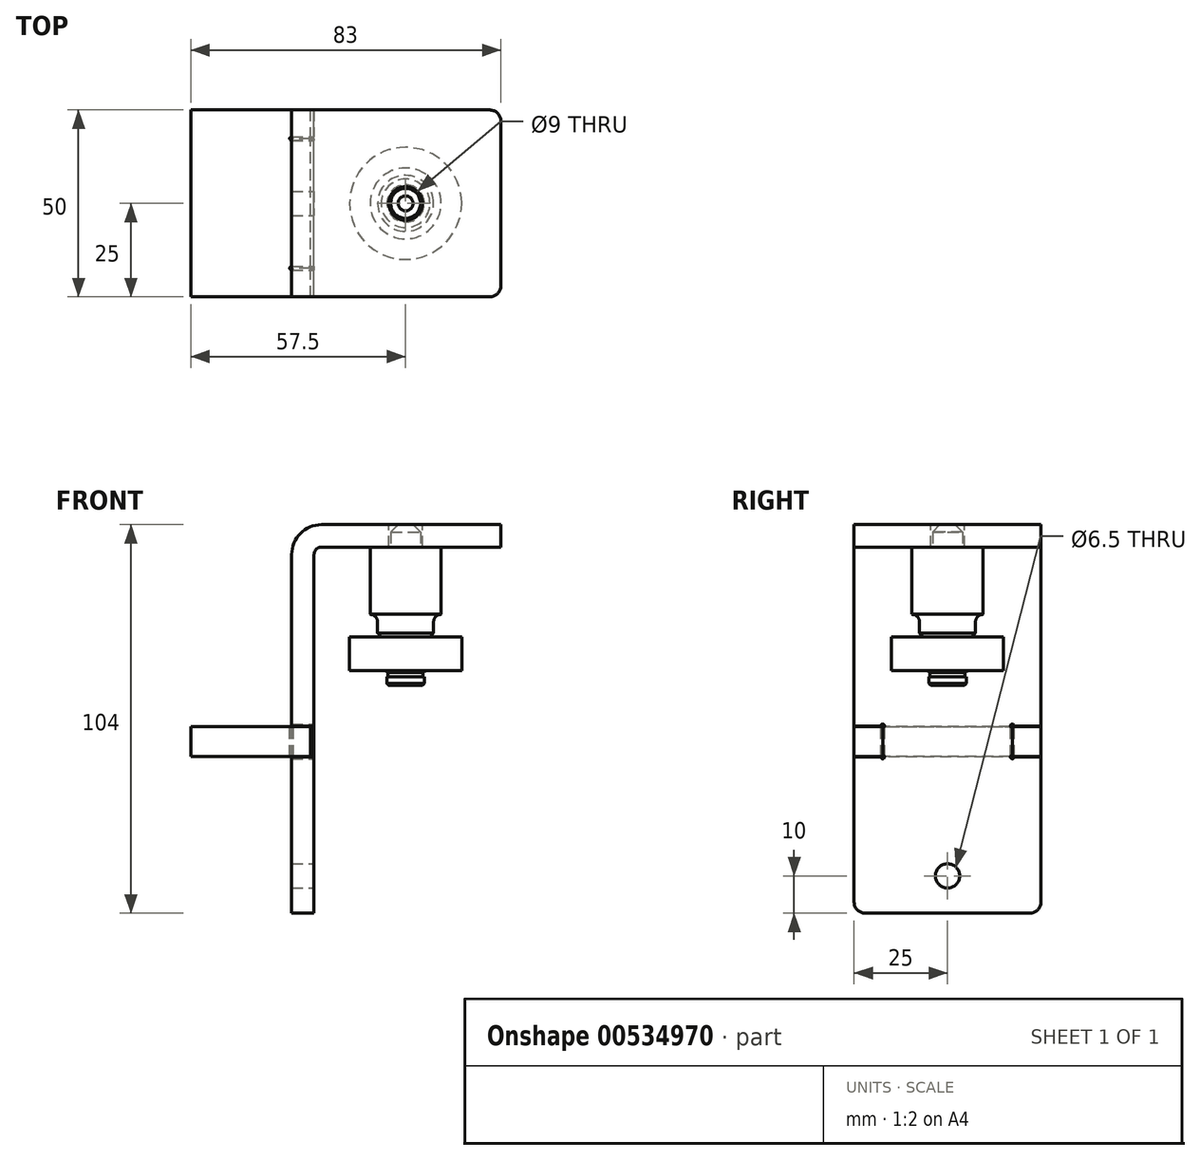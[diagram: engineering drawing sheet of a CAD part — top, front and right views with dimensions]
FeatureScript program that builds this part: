
annotation { "Feature Type Name" : "Feature", "Feature Type Description" : "" }
export const myFeature = defineFeature(function(context is Context, id is Id, definition is map)
    precondition{}
    {
        {
            var Q0;
            Q0=qCreatedBy(makeId("Front.planeOp"),FACE);
            var sketch = newSketch(context, id + "F0", { "sketchPlane" : qUnion([Q0])});
            skLineSegment(sketch, "E0", {"start": v(0, 0) * mm, "end": v(0, 96) * mm});
            skLineSegment(sketch, "E1", {"start": v(8, 104) * mm, "end": v(56, 104) * mm});
            skLineSegment(sketch, "E2", {"start": v(56, 104) * mm, "end": v(56, 98) * mm});
            skLineSegment(sketch, "E3", {"start": v(56, 98) * mm, "end": v(8, 98) * mm});
            skLineSegment(sketch, "E4", {"start": v(6, 96) * mm, "end": v(6, 0) * mm});
            skLineSegment(sketch, "E5", {"start": v(6, 0) * mm, "end": v(0, 0) * mm});
            skPoint(sketch, "E6.visualSharp", {"position": v(0, 104) * mm});
            skArc(sketch, "E6.filletArc", {"start": v(8, 104) * mm, "mid": v(2.34, 101.66) * mm, "end": v(0, 96) * mm});
            skPoint(sketch, "E7.visualSharp", {"position": v(6, 98) * mm});
            skArc(sketch, "E7.filletArc", {"start": v(8, 98) * mm, "mid": v(6.59, 97.41) * mm, "end": v(6, 96) * mm});
            skSolve(sketch);
        }
        {
            var Q0;
            Q0 = qSketchRegion(id + "F0", true);
            extrude(context, id + "F1", {"entities" : qUnion([Q0]), "depth" : 50 * mm, "offsetDistance" : 25 * mm, "symmetric" : true});
        }
        {
            var Q0;
            Q0=makeQuery(id+"F1.opExtrude","CAP_EDGE",EDGE,{"disambiguationData":[OSD([sQuery(id+"F0.wireOp",EDGE,"E5")])],"isStart":false});
            var Q1;
            Q1=makeQuery(id+"F1.opExtrude","CAP_EDGE",EDGE,{"disambiguationData":[OSD([sQuery(id+"F0.wireOp",EDGE,"E5")])],"isStart":true});
            var Q2;
            Q2=makeQuery(id+"F1.opExtrude","CAP_EDGE",EDGE,{"disambiguationData":[OSD([sQuery(id+"F0.wireOp",EDGE,"E2")])],"isStart":false});
            var Q3;
            Q3=makeQuery(id+"F1.opExtrude","CAP_EDGE",EDGE,{"disambiguationData":[OSD([sQuery(id+"F0.wireOp",EDGE,"E2")])],"isStart":true});
            fillet(context, id + "F2", {"entities" : qUnion([Q0, Q1, Q2, Q3]), "radius" : 3 * mm, "tangentPropagation" : true, "allowEdgeOverflow" : false});
        }
        {
            var Q0;
            Q0=makeQuery(id+"F1.opExtrude","SWEPT_FACE",FACE,{"disambiguationData":[OSD([sQuery(id+"F0.wireOp",EDGE,"E4")])]});
            var sketch = newSketch(context, id + "F3", { "sketchPlane" : qUnion([Q0])});
            skLineSegment(sketch, "E8.bottom", {"start": v(-25, 41.85) * mm, "end": v(-17.35, 41.85) * mm});
            skLineSegment(sketch, "E8.top", {"start": v(-25, 50.15) * mm, "end": v(-17.35, 50.15) * mm});
            skLineSegment(sketch, "E8.left", {"start": v(-25, 41.85) * mm, "end": v(-25, 50.15) * mm});
            skLineSegment(sketch, "E8.right", {"start": v(-17.35, 41.85) * mm, "end": v(-17.35, 50.15) * mm});
            skCircle(sketch, "E9", {"center": v(-17.35, 50.15) * mm, "radius": 0.5 * mm});
            skLineSegment(sketch, "E10", {"start": v(0, 0) * mm, "end": v(0, 90.28) * mm, "construction": true});
            skPoint(sketch, "E10.endSnap0", {"position": v(0, 0) * mm});
            skCircle(sketch, "E11", {"center": v(-17.35, 41.85) * mm, "radius": 0.5 * mm});
            skLineSegment(sketch, "E12.MirrorCS", {"start": v(25, 50.15) * mm, "end": v(17.35, 50.15) * mm});
            skLineSegment(sketch, "E13.MirrorCS", {"start": v(25, 41.85) * mm, "end": v(17.35, 41.85) * mm});
            skLineSegment(sketch, "E14.MirrorCS", {"start": v(25, 41.85) * mm, "end": v(25, 50.15) * mm});
            skCircle(sketch, "E15.MirrorC", {"center": v(17.35, 41.85) * mm, "radius": 0.5 * mm});
            skCircle(sketch, "E16.MirrorC", {"center": v(17.35, 50.15) * mm, "radius": 0.5 * mm});
            skLineSegment(sketch, "E17.MirrorCS", {"start": v(17.35, 41.85) * mm, "end": v(17.35, 50.15) * mm});
            skSolve(sketch);
        }
        {
            var Q0;
            {var subQ5=sQuery(id+"F3.wireOp",EDGE,"E8.left");Q0=makeQuery(id+"F3.imprint","IMPRINT",FACE,{"disambiguationData":[TD([[makeQuery(id+"F3.imprint","IMPRINT",EDGE,{"derivedFrom":subQ5}),1.0]])]});}
            var Q1;
            {var subQ0=sQuery(id+"F3.wireOp",EDGE,"E8.right");var subQ1=sQuery(id+"F3.wireOp",EDGE,"E8.top");var subQ2=makeQuery(id+"F3.imprint","INTERSECT",VERTEX,{"derivedFrom":[subQ1,subQ0]});Q1=makeQuery(id+"F3.imprint","IMPRINT",FACE,{"disambiguationData":[TD([[makeQuery(id+"F3.imprint","IMPRINT",EDGE,{"disambiguationData":[TD([[subQ2,1.0]])],"derivedFrom":subQ1}),-1.0]])]});}
            var Q2;
            {var subQ0=sQuery(id+"F3.wireOp",EDGE,"E8.right");var subQ1=sQuery(id+"F3.wireOp",EDGE,"E8.top");var subQ2=makeQuery(id+"F3.imprint","INTERSECT",VERTEX,{"derivedFrom":[subQ1,subQ0]});Q2=makeQuery(id+"F3.imprint","IMPRINT",FACE,{"disambiguationData":[TD([[makeQuery(id+"F3.imprint","IMPRINT",EDGE,{"disambiguationData":[TD([[subQ2,1.0]])],"derivedFrom":subQ1}),1.0]])]});}
            var Q3;
            {var subQ0=sQuery(id+"F3.wireOp",EDGE,"E8.right");var subQ1=sQuery(id+"F3.wireOp",EDGE,"E8.bottom");var subQ2=makeQuery(id+"F3.imprint","INTERSECT",VERTEX,{"derivedFrom":[subQ1,subQ0]});Q3=makeQuery(id+"F3.imprint","IMPRINT",FACE,{"disambiguationData":[TD([[makeQuery(id+"F3.imprint","IMPRINT",EDGE,{"disambiguationData":[TD([[subQ2,1.0]])],"derivedFrom":subQ1}),1.0]])]});}
            var Q4;
            {var subQ0=sQuery(id+"F3.wireOp",EDGE,"E8.right");var subQ1=sQuery(id+"F3.wireOp",EDGE,"E8.bottom");var subQ2=makeQuery(id+"F3.imprint","INTERSECT",VERTEX,{"derivedFrom":[subQ1,subQ0]});Q4=makeQuery(id+"F3.imprint","IMPRINT",FACE,{"disambiguationData":[TD([[makeQuery(id+"F3.imprint","IMPRINT",EDGE,{"disambiguationData":[TD([[subQ2,1.0]])],"derivedFrom":subQ1}),-1.0]])]});}
            var Q5;
            {var subQ0=sQuery(id+"F3.wireOp",EDGE,"E14.MirrorCS");Q5=makeQuery(id+"F3.imprint","IMPRINT",FACE,{"disambiguationData":[TD([[makeQuery(id+"F3.imprint","IMPRINT",EDGE,{"derivedFrom":subQ0}),-1.0]])]});}
            var Q6;
            {var subQ0=sQuery(id+"F3.wireOp",EDGE,"E17.MirrorCS");var subQ1=sQuery(id+"F3.wireOp",EDGE,"E12.MirrorCS");var subQ2=makeQuery(id+"F3.imprint","INTERSECT",VERTEX,{"derivedFrom":[subQ1,subQ0]});Q6=makeQuery(id+"F3.imprint","IMPRINT",FACE,{"disambiguationData":[TD([[makeQuery(id+"F3.imprint","IMPRINT",EDGE,{"disambiguationData":[TD([[subQ2,1.0]])],"derivedFrom":subQ1}),-1.0]])]});}
            var Q7;
            {var subQ0=sQuery(id+"F3.wireOp",EDGE,"E17.MirrorCS");var subQ1=sQuery(id+"F3.wireOp",EDGE,"E13.MirrorCS");var subQ2=makeQuery(id+"F3.imprint","INTERSECT",VERTEX,{"derivedFrom":[subQ1,subQ0]});Q7=makeQuery(id+"F3.imprint","IMPRINT",FACE,{"disambiguationData":[TD([[makeQuery(id+"F3.imprint","IMPRINT",EDGE,{"disambiguationData":[TD([[subQ2,1.0]])],"derivedFrom":subQ1}),1.0]])]});}
            var Q8;
            {var subQ0=sQuery(id+"F3.wireOp",EDGE,"E17.MirrorCS");var subQ1=sQuery(id+"F3.wireOp",EDGE,"E12.MirrorCS");var subQ2=makeQuery(id+"F3.imprint","INTERSECT",VERTEX,{"derivedFrom":[subQ1,subQ0]});Q8=makeQuery(id+"F3.imprint","IMPRINT",FACE,{"disambiguationData":[TD([[makeQuery(id+"F3.imprint","IMPRINT",EDGE,{"disambiguationData":[TD([[subQ2,1.0]])],"derivedFrom":subQ1}),1.0]])]});}
            var Q9;
            {var subQ0=sQuery(id+"F3.wireOp",EDGE,"E17.MirrorCS");var subQ1=sQuery(id+"F3.wireOp",EDGE,"E13.MirrorCS");var subQ2=makeQuery(id+"F3.imprint","INTERSECT",VERTEX,{"derivedFrom":[subQ1,subQ0]});Q9=makeQuery(id+"F3.imprint","IMPRINT",FACE,{"disambiguationData":[TD([[makeQuery(id+"F3.imprint","IMPRINT",EDGE,{"disambiguationData":[TD([[subQ2,1.0]])],"derivedFrom":subQ1}),-1.0]])]});}
            extrude(context, id + "F4", {"entities" : qUnion([Q0, Q1, Q2, Q3, Q4, Q5, Q6, Q7, Q8, Q9]), "operationType" : NewBodyOperationType.REMOVE, "oppositeDirection" : true, "depth" : 25 * mm, "offsetDistance" : 25 * mm});
        }
        {
            var Q0;
            Q0=makeQuery(id+"F1.opExtrude","SWEPT_FACE",FACE,{"disambiguationData":[OSD([sQuery(id+"F0.wireOp",EDGE,"E1")])]});
            var sketch = newSketch(context, id + "F5", { "sketchPlane" : qUnion([Q0])});
            skCircle(sketch, "E18", {"center": v(30.5, 0) * mm, "radius": 4.5 * mm});
            skPoint(sketch, "E18.centerSnap0", {"position": v(56, 0) * mm});
            skPoint(sketch, "E18.centerSnap1", {"position": v(30.5, -25) * mm});
            skSolve(sketch);
        }
        {
            var Q0;
            Q0 = qSketchRegion(id + "F5", true);
            extrude(context, id + "F6", {"entities" : qUnion([Q0]), "operationType" : NewBodyOperationType.REMOVE, "endBound" : BoundingType.UP_TO_NEXT, "oppositeDirection" : true, "depth" : 25 * mm, "offsetDistance" : 25 * mm});
        }
        {
            var Q0;
            Q0=makeQuery(id+"F1.opExtrude","CAP_EDGE",EDGE,{"disambiguationData":[OSD([sQuery(id+"F0.wireOp",EDGE,"E1")])],"isStart":false});
            cPoint(context, id + "F7", {"entities" : qUnion([Q0]), "parameter" : 0.5});
        }
        {
            var Q0;
            Q0=qCreatedBy(makeId("Right.planeOp"),FACE);
            var Q1;
            Q1 = qCreatedBy(id + "F7" ,VERTEX);
            cPlane(context, id + "F8", {"entities" : qUnion([Q0, Q1]), "cplaneType" : CPlaneType.PLANE_POINT, "offset" : 25 * mm, "width" : 150 * mm, "height" : 150 * mm});
        }
        {
            var Q0;
            Q0=qCreatedBy(id+"F8.planeOp",FACE);
            var sketch = newSketch(context, id + "F9", { "sketchPlane" : qUnion([Q0])});
            skLineSegment(sketch, "E19", {"start": v(0, 104) * mm, "end": v(0, 55.5) * mm, "construction": true});
            skLineSegment(sketch, "E20", {"start": v(0, 104) * mm, "end": v(-2, 104) * mm});
            skLineSegment(sketch, "E21", {"start": v(-2, 104) * mm, "end": v(-4, 102) * mm});
            skLineSegment(sketch, "E22", {"start": v(-4, 102) * mm, "end": v(-4, 98) * mm});
            skLineSegment(sketch, "E23", {"start": v(-4, 98) * mm, "end": v(-9.5, 98) * mm});
            skLineSegment(sketch, "E24", {"start": v(-9.5, 98) * mm, "end": v(-9.5, 80) * mm});
            skLineSegment(sketch, "E25", {"start": v(-9.5, 80) * mm, "end": v(-9.5, 80) * mm});
            skLineSegment(sketch, "E26", {"start": v(-7.5, 78) * mm, "end": v(-7.5, 75) * mm});
            skLineSegment(sketch, "E27", {"start": v(-7.5, 75) * mm, "end": v(-6.5, 74) * mm});
            skLineSegment(sketch, "E28", {"start": v(-6.5, 74) * mm, "end": v(-5, 74) * mm});
            skLineSegment(sketch, "E29", {"start": v(-5, 74) * mm, "end": v(-5, 64.5) * mm});
            skLineSegment(sketch, "E30", {"start": v(-5, 64.5) * mm, "end": v(-4.7, 64.5) * mm});
            skLineSegment(sketch, "E31", {"start": v(-4.7, 64.5) * mm, "end": v(-4.7, 63.3) * mm});
            skLineSegment(sketch, "E32", {"start": v(-4.7, 63.3) * mm, "end": v(-5, 63.3) * mm});
            skLineSegment(sketch, "E33", {"start": v(-5, 63.3) * mm, "end": v(-5, 61.5) * mm});
            skLineSegment(sketch, "E34", {"start": v(-5, 61.5) * mm, "end": v(-4.5, 61) * mm});
            skLineSegment(sketch, "E35", {"start": v(-4.5, 61) * mm, "end": v(0, 61) * mm});
            skLineSegment(sketch, "E36", {"start": v(0, 61) * mm, "end": v(0, 104) * mm});
            skPoint(sketch, "E37.visualSharp", {"position": v(-7.5, 80) * mm});
            skArc(sketch, "E37.filletArc", {"start": v(-7.5, 78) * mm, "mid": v(-8.09, 79.41) * mm, "end": v(-9.5, 80) * mm});
            skLineSegment(sketch, "E38.bottom", {"start": v(-5, 73.9) * mm, "end": v(-15, 73.9) * mm});
            skLineSegment(sketch, "E38.top", {"start": v(-5, 64.9) * mm, "end": v(-15, 64.9) * mm});
            skLineSegment(sketch, "E38.left", {"start": v(-5, 73.9) * mm, "end": v(-5, 64.9) * mm});
            skLineSegment(sketch, "E38.right", {"start": v(-15, 73.9) * mm, "end": v(-15, 64.9) * mm});
            skSolve(sketch);
        }
        {
            var Q0;
            Q0 = qSketchRegion(id + "F9", true);
            var Q1;
            Q1=sQuery(id+"F9.wireOp",EDGE,"E36");
            revolve(context, id + "F10", {"entities" : qUnion([Q0]), "axis" : qUnion([Q1]), "revolveType" : RevolveType.FULL});
        }
        {
            var Q0;
            Q0=makeQuery(id+"F4.boolean.opBoolean","COPY",FACE,{"derivedFrom":makeQuery(id+"F4.opExtrude","SWEPT_FACE",FACE,{"disambiguationData":[OSD([sQuery(id+"F3.wireOp",EDGE,"E8.top")])]})});
            cPlane(context, id + "F11", {"entities" : qUnion([Q0]), "cplaneType" : CPlaneType.OFFSET, "offset" : 0.15 * mm, "width" : 150 * mm, "height" : 150 * mm});
        }
        {
            var Q0;
            Q0=qCreatedBy(id+"F11.planeOp",FACE);
            var sketch = newSketch(context, id + "F12", { "sketchPlane" : qUnion([Q0])});
            skLineSegment(sketch, "E39.bottom", {"start": v(-27, 25) * mm, "end": v(5, 25) * mm});
            skLineSegment(sketch, "E39.top", {"start": v(-27, -25) * mm, "end": v(5, -25) * mm});
            skLineSegment(sketch, "E39.left", {"start": v(5, 25) * mm, "end": v(5, -25) * mm});
            skLineSegment(sketch, "E39.right", {"start": v(-27, 25) * mm, "end": v(-27, -25) * mm});
            skPoint(sketch, "E39.middle", {"position": v(-11, 0) * mm});
            skSolve(sketch);
        }
        {
            var Q0;
            Q0 = qSketchRegion(id + "F12", true);
            extrude(context, id + "F13", {"entities" : qUnion([Q0]), "depth" : 8 * mm, "offsetDistance" : 25 * mm});
        }
        {
            var Q0;
            Q0=makeQuery(id+"F13.opExtrude","CAP_FACE",FACE,{"disambiguationData":[OSD([sQuery(id+"F12.wireOp",EDGE,"E39.bottom"),sQuery(id+"F12.wireOp",EDGE,"E39.top"),sQuery(id+"F12.wireOp",EDGE,"E39.left"),sQuery(id+"F12.wireOp",EDGE,"E39.right")])],"isStart":true});
            var sketch = newSketch(context, id + "F14", { "sketchPlane" : qUnion([Q0])});
            skLineSegment(sketch, "E40.bottom", {"start": v(6, 17.35) * mm, "end": v(0, 17.35) * mm});
            skLineSegment(sketch, "E40.top", {"start": v(6, -17.35) * mm, "end": v(0, -17.35) * mm});
            skLineSegment(sketch, "E40.left", {"start": v(6, 17.35) * mm, "end": v(6, -17.35) * mm});
            skLineSegment(sketch, "E40.right", {"start": v(0, 17.35) * mm, "end": v(0, -17.35) * mm});
            skCircle(sketch, "E41", {"center": v(0, 17.35) * mm, "radius": 0.5 * mm});
            skCircle(sketch, "E42", {"center": v(0, -17.35) * mm, "radius": 0.5 * mm});
            skSolve(sketch);
        }
        {
            var Q0;
            {var subQ0=sQuery(id+"F14.wireOp",EDGE,"E40.right");var subQ1=sQuery(id+"F14.wireOp",EDGE,"E40.top");var subQ2=makeQuery(id+"F14.imprint","INTERSECT",VERTEX,{"derivedFrom":[subQ1,subQ0]});Q0=makeQuery(id+"F14.imprint","IMPRINT",FACE,{"disambiguationData":[TD([[makeQuery(id+"F14.imprint","IMPRINT",EDGE,{"disambiguationData":[TD([[subQ2,1.0]])],"derivedFrom":subQ1}),1.0]])]});}
            var Q1;
            {var subQ0=sQuery(id+"F14.wireOp",EDGE,"E40.right");var subQ1=sQuery(id+"F14.wireOp",EDGE,"E40.top");var subQ2=makeQuery(id+"F14.imprint","INTERSECT",VERTEX,{"derivedFrom":[subQ1,subQ0]});Q1=makeQuery(id+"F14.imprint","IMPRINT",FACE,{"disambiguationData":[TD([[makeQuery(id+"F14.imprint","IMPRINT",EDGE,{"disambiguationData":[TD([[subQ2,1.0]])],"derivedFrom":subQ1}),-1.0]])]});}
            var Q2;
            {var subQ0=sQuery(id+"F14.wireOp",EDGE,"E41");var subQ5=sQuery(id+"F14.wireOp",EDGE,"E40.bottom");var subQ11=makeQuery(id+"F14.imprint","INTERSECT",VERTEX,{"derivedFrom":[subQ5,subQ0]});Q2=makeQuery(id+"F14.imprint","IMPRINT",FACE,{"disambiguationData":[TD([[makeQuery(id+"F14.imprint","IMPRINT",EDGE,{"disambiguationData":[TD([[subQ11,1.0]])],"derivedFrom":subQ5}),1.0]])]});}
            var Q3;
            {var subQ0=sQuery(id+"F14.wireOp",EDGE,"E40.right");var subQ1=sQuery(id+"F14.wireOp",EDGE,"E40.bottom");var subQ2=makeQuery(id+"F14.imprint","INTERSECT",VERTEX,{"derivedFrom":[subQ1,subQ0]});Q3=makeQuery(id+"F14.imprint","IMPRINT",FACE,{"disambiguationData":[TD([[makeQuery(id+"F14.imprint","IMPRINT",EDGE,{"disambiguationData":[TD([[subQ2,1.0]])],"derivedFrom":subQ1}),-1.0]])]});}
            var Q4;
            {var subQ0=sQuery(id+"F14.wireOp",EDGE,"E40.right");var subQ1=sQuery(id+"F14.wireOp",EDGE,"E40.bottom");var subQ2=makeQuery(id+"F14.imprint","INTERSECT",VERTEX,{"derivedFrom":[subQ1,subQ0]});Q4=makeQuery(id+"F14.imprint","IMPRINT",FACE,{"disambiguationData":[TD([[makeQuery(id+"F14.imprint","IMPRINT",EDGE,{"disambiguationData":[TD([[subQ2,1.0]])],"derivedFrom":subQ1}),1.0]])]});}
            extrude(context, id + "F15", {"entities" : qUnion([Q0, Q1, Q2, Q3, Q4]), "operationType" : NewBodyOperationType.REMOVE, "endBound" : BoundingType.UP_TO_NEXT, "oppositeDirection" : true, "depth" : 8 * mm, "offsetDistance" : 25 * mm});
        }
        {
            var Q0;
            {var subQ0=sQuery(id+"F0.wireOp",EDGE,"E5");var subQ3=sQuery(id+"F0.wireOp",EDGE,"E4");Q0=makeQuery(id+"F15.boolean.opBoolean","SPLIT",FACE,{"disambiguationData":[TD([makeQuery(id+"F1.opExtrude","SWEPT_FACE",FACE,{"disambiguationData":[OSD([subQ0])]})])],"derivedFrom":makeQuery(id+"F1.opExtrude","SWEPT_FACE",FACE,{"disambiguationData":[OSD([subQ3])]})});}
            var sketch = newSketch(context, id + "F16", { "sketchPlane" : qUnion([Q0])});
            skCircle(sketch, "E43", {"center": v(0, 10) * mm, "radius": 3.25 * mm});
            skPoint(sketch, "E43.centerSnap0", {"position": v(0, 0) * mm});
            skSolve(sketch);
        }
        {
            var Q0;
            Q0 = qSketchRegion(id + "F16", true);
            extrude(context, id + "F17", {"entities" : qUnion([Q0]), "operationType" : NewBodyOperationType.REMOVE, "oppositeDirection" : true, "depth" : 25 * mm, "offsetDistance" : 25 * mm});
        }
    });
